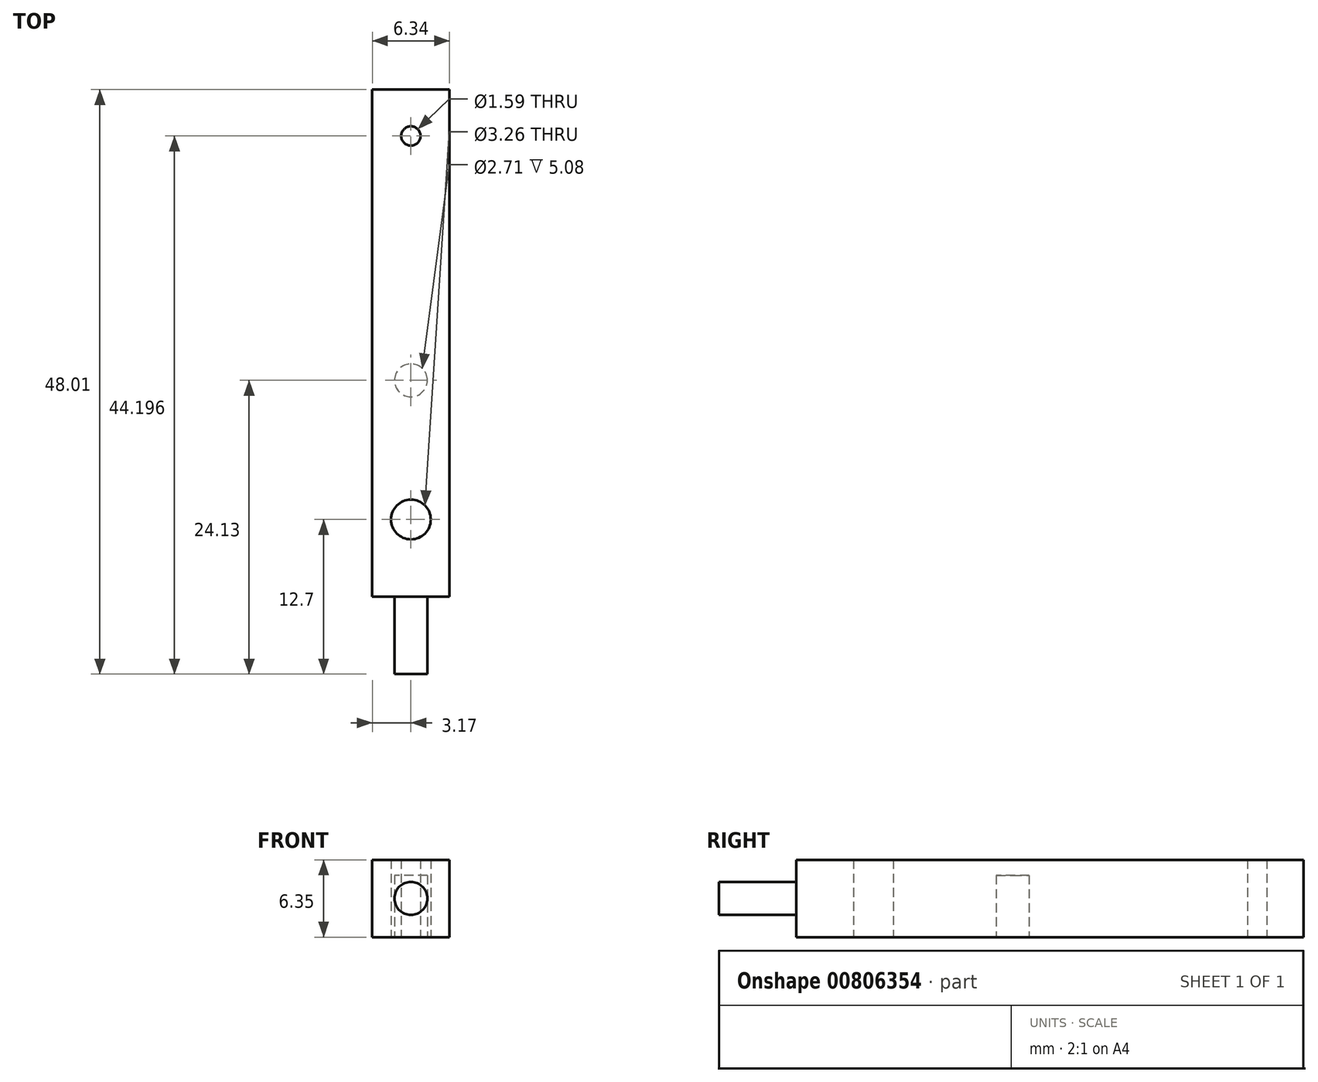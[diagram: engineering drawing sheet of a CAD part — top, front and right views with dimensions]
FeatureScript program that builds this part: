
annotation { "Feature Type Name" : "Feature", "Feature Type Description" : "" }
export const myFeature = defineFeature(function(context is Context, id is Id, definition is map)
    precondition{}
    {
        {
            var Q0;
            Q0=qCreatedBy(makeId("Top.planeOp"),FACE);
            var sketch = newSketch(context, id + "F0", { "sketchPlane" : qUnion([Q0])});
            skLineSegment(sketch, "E0.bottom", {"start": v(-3.17, 12.7) * mm, "end": v(3.18, 12.7) * mm});
            skLineSegment(sketch, "E0.top", {"start": v(-3.18, -12.7) * mm, "end": v(3.17, -12.7) * mm});
            skLineSegment(sketch, "E0.left", {"start": v(-3.17, 12.7) * mm, "end": v(-3.18, -12.7) * mm});
            skLineSegment(sketch, "E0.right", {"start": v(3.18, 12.7) * mm, "end": v(3.17, -12.7) * mm});
            skPoint(sketch, "E0.middle", {"position": v(0, 0) * mm});
            skCircle(sketch, "E1", {"center": v(0, -6.35) * mm, "radius": 1.63 * mm});
            skCircle(sketch, "E2", {"center": v(0, 5.08) * mm, "radius": 1.35 * mm});
            skLineSegment(sketch, "E3.bottom", {"start": v(3.18, 12.7) * mm, "end": v(-3.17, 12.7) * mm});
            skLineSegment(sketch, "E3.left", {"start": v(3.18, 12.7) * mm, "end": v(3.18, 25.15) * mm});
            skLineSegment(sketch, "E3.right", {"start": v(-3.17, 12.7) * mm, "end": v(-3.17, 25.15) * mm});
            skCircle(sketch, "E4", {"center": v(0, 25.15) * mm, "radius": 0.8 * mm});
            skLineSegment(sketch, "E5.top", {"start": v(-3.17, 28.96) * mm, "end": v(3.18, 28.96) * mm});
            skLineSegment(sketch, "E5.left", {"start": v(-3.17, 25.15) * mm, "end": v(-3.17, 28.96) * mm});
            skLineSegment(sketch, "E5.right", {"start": v(3.18, 25.15) * mm, "end": v(3.18, 28.96) * mm});
            skSolve(sketch);
        }
        {
            var Q0;
            Q0 = qSketchRegion(id + "F0", true);
            var Q1;
            Q1=makeQuery(id+"F0.imprint","IMPRINT",FACE,{"disambiguationData":[TD([[makeQuery(id+"F0.imprint","IMPRINT",EDGE,{"derivedFrom":sQuery(id+"F0.wireOp",EDGE,"E2")}),1.0]])]});
            extrude(context, id + "F1", {"entities" : qUnion([Q0, Q1]), "depth" : 6.35 * mm, "offsetDistance" : 25.4 * mm});
        }
        {
            var Q0;
            Q0=makeQuery(id+"F0.imprint","IMPRINT",FACE,{"disambiguationData":[TD([[makeQuery(id+"F0.imprint","IMPRINT",EDGE,{"derivedFrom":sQuery(id+"F0.wireOp",EDGE,"E2")}),1.0]])]});
            extrude(context, id + "F2", {"entities" : qUnion([Q0]), "operationType" : NewBodyOperationType.REMOVE, "depth" : 5.08 * mm, "offsetDistance" : 25.4 * mm});
        }
        {
            var Q0;
            Q0=makeQuery(id+"F1.opExtrude","SWEPT_FACE",FACE,{"disambiguationData":[OSD([sQuery(id+"F0.wireOp",EDGE,"E0.top")])]});
            var sketch = newSketch(context, id + "F3", { "sketchPlane" : qUnion([Q0])});
            skCircle(sketch, "E6", {"center": v(0, 3.18) * mm, "radius": 1.35 * mm});
            skPoint(sketch, "E6.centerSnap0", {"position": v(-3.18, 3.18) * mm});
            skSolve(sketch);
        }
        {
            var Q0;
            Q0 = qSketchRegion(id + "F3", true);
            extrude(context, id + "F4", {"entities" : qUnion([Q0]), "operationType" : NewBodyOperationType.ADD, "depth" : 6.35 * mm, "offsetDistance" : 25.4 * mm});
        }
    });
